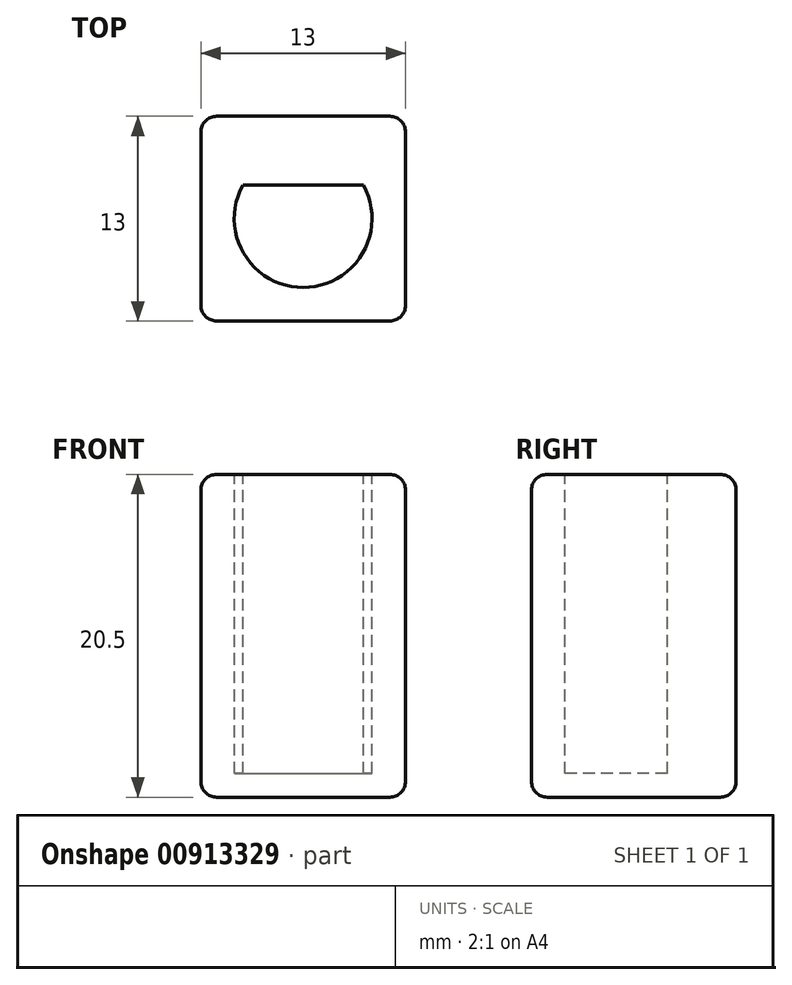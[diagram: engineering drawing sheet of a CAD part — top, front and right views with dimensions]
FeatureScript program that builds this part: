
annotation { "Feature Type Name" : "Feature", "Feature Type Description" : "" }
export const myFeature = defineFeature(function(context is Context, id is Id, definition is map)
    precondition{}
    {
        {
            var Q0;
            Q0=qCreatedBy(makeId("Top.planeOp"),FACE);
            var sketch = newSketch(context, id + "F0", { "sketchPlane" : qUnion([Q0])});
            skLineSegment(sketch, "E0.bottom", {"start": v(6.5, 6.5) * mm, "end": v(-6.5, 6.5) * mm});
            skLineSegment(sketch, "E0.top", {"start": v(6.5, -6.5) * mm, "end": v(-6.5, -6.5) * mm});
            skLineSegment(sketch, "E0.left", {"start": v(6.5, 6.5) * mm, "end": v(6.5, -6.5) * mm});
            skLineSegment(sketch, "E0.right", {"start": v(-6.5, 6.5) * mm, "end": v(-6.5, -6.5) * mm});
            skPoint(sketch, "E0.middle", {"position": v(0, 0) * mm});
            skSolve(sketch);
        }
        {
            var Q0;
            Q0 = qSketchRegion(id + "F0", true);
            extrude(context, id + "F1", {"entities" : qUnion([Q0]), "depth" : 20.5 * mm, "offsetDistance" : 25 * mm});
        }
        {
            var Q0;
            Q0=makeQuery(id+"F1.opExtrude","CAP_FACE",FACE,{"disambiguationData":[OSD([sQuery(id+"F0.wireOp",EDGE,"E0.bottom"),sQuery(id+"F0.wireOp",EDGE,"E0.top"),sQuery(id+"F0.wireOp",EDGE,"E0.left"),sQuery(id+"F0.wireOp",EDGE,"E0.right")])],"isStart":false});
            var sketch = newSketch(context, id + "F2", { "sketchPlane" : qUnion([Q0])});
            skArc(sketch, "E1", {"start": v(-3.82, 2.12) * mm, "mid": v(0, -4.38) * mm, "end": v(3.82, 2.13) * mm});
            skLineSegment(sketch, "E2", {"start": v(-3.82, 2.12) * mm, "end": v(3.82, 2.13) * mm});
            skSolve(sketch);
        }
        {
            var Q0;
            Q0 = qSketchRegion(id + "F2", true);
            extrude(context, id + "F3", {"entities" : qUnion([Q0]), "operationType" : NewBodyOperationType.REMOVE, "oppositeDirection" : true, "depth" : 19 * mm, "offsetDistance" : 25 * mm});
        }
        {
            var Q0;
            Q0=makeQuery(id+"F1.opExtrude","SWEPT_EDGE",EDGE,{"disambiguationData":[OSD([sQuery(id+"F0.wireOp",EDGE,"E0.bottom"),sQuery(id+"F0.wireOp",EDGE,"E0.right")])]});
            var Q1;
            Q1=makeQuery(id+"F1.opExtrude","SWEPT_EDGE",EDGE,{"disambiguationData":[OSD([sQuery(id+"F0.wireOp",EDGE,"E0.top"),sQuery(id+"F0.wireOp",EDGE,"E0.right")])]});
            var Q2;
            Q2=makeQuery(id+"F1.opExtrude","SWEPT_EDGE",EDGE,{"disambiguationData":[OSD([sQuery(id+"F0.wireOp",EDGE,"E0.top"),sQuery(id+"F0.wireOp",EDGE,"E0.left")])]});
            var Q3;
            Q3=makeQuery(id+"F1.opExtrude","SWEPT_EDGE",EDGE,{"disambiguationData":[OSD([sQuery(id+"F0.wireOp",EDGE,"E0.bottom"),sQuery(id+"F0.wireOp",EDGE,"E0.left")])]});
            var Q4;
            Q4=makeQuery(id+"F1.opExtrude","CAP_EDGE",EDGE,{"disambiguationData":[OSD([sQuery(id+"F0.wireOp",EDGE,"E0.bottom")])],"isStart":true});
            var Q5;
            Q5=makeQuery(id+"F1.opExtrude","CAP_EDGE",EDGE,{"disambiguationData":[OSD([sQuery(id+"F0.wireOp",EDGE,"E0.right")])],"isStart":true});
            var Q6;
            Q6=makeQuery(id+"F1.opExtrude","CAP_EDGE",EDGE,{"disambiguationData":[OSD([sQuery(id+"F0.wireOp",EDGE,"E0.left")])],"isStart":true});
            var Q7;
            Q7=makeQuery(id+"F1.opExtrude","CAP_EDGE",EDGE,{"disambiguationData":[OSD([sQuery(id+"F0.wireOp",EDGE,"E0.top")])],"isStart":true});
            var Q8;
            Q8=makeQuery(id+"F1.opExtrude","CAP_EDGE",EDGE,{"disambiguationData":[OSD([sQuery(id+"F0.wireOp",EDGE,"E0.top")])],"isStart":false});
            var Q9;
            Q9=makeQuery(id+"F1.opExtrude","CAP_EDGE",EDGE,{"disambiguationData":[OSD([sQuery(id+"F0.wireOp",EDGE,"E0.left")])],"isStart":false});
            var Q10;
            Q10=makeQuery(id+"F1.opExtrude","CAP_EDGE",EDGE,{"disambiguationData":[OSD([sQuery(id+"F0.wireOp",EDGE,"E0.bottom")])],"isStart":false});
            var Q11;
            Q11=makeQuery(id+"F1.opExtrude","CAP_EDGE",EDGE,{"disambiguationData":[OSD([sQuery(id+"F0.wireOp",EDGE,"E0.right")])],"isStart":false});
            fillet(context, id + "F4", {"entities" : qUnion([Q0, Q1, Q2, Q3, Q4, Q5, Q6, Q7, Q8, Q9, Q10, Q11]), "radius" : 1 * mm, "tangentPropagation" : true, "allowEdgeOverflow" : false});
        }
    });
